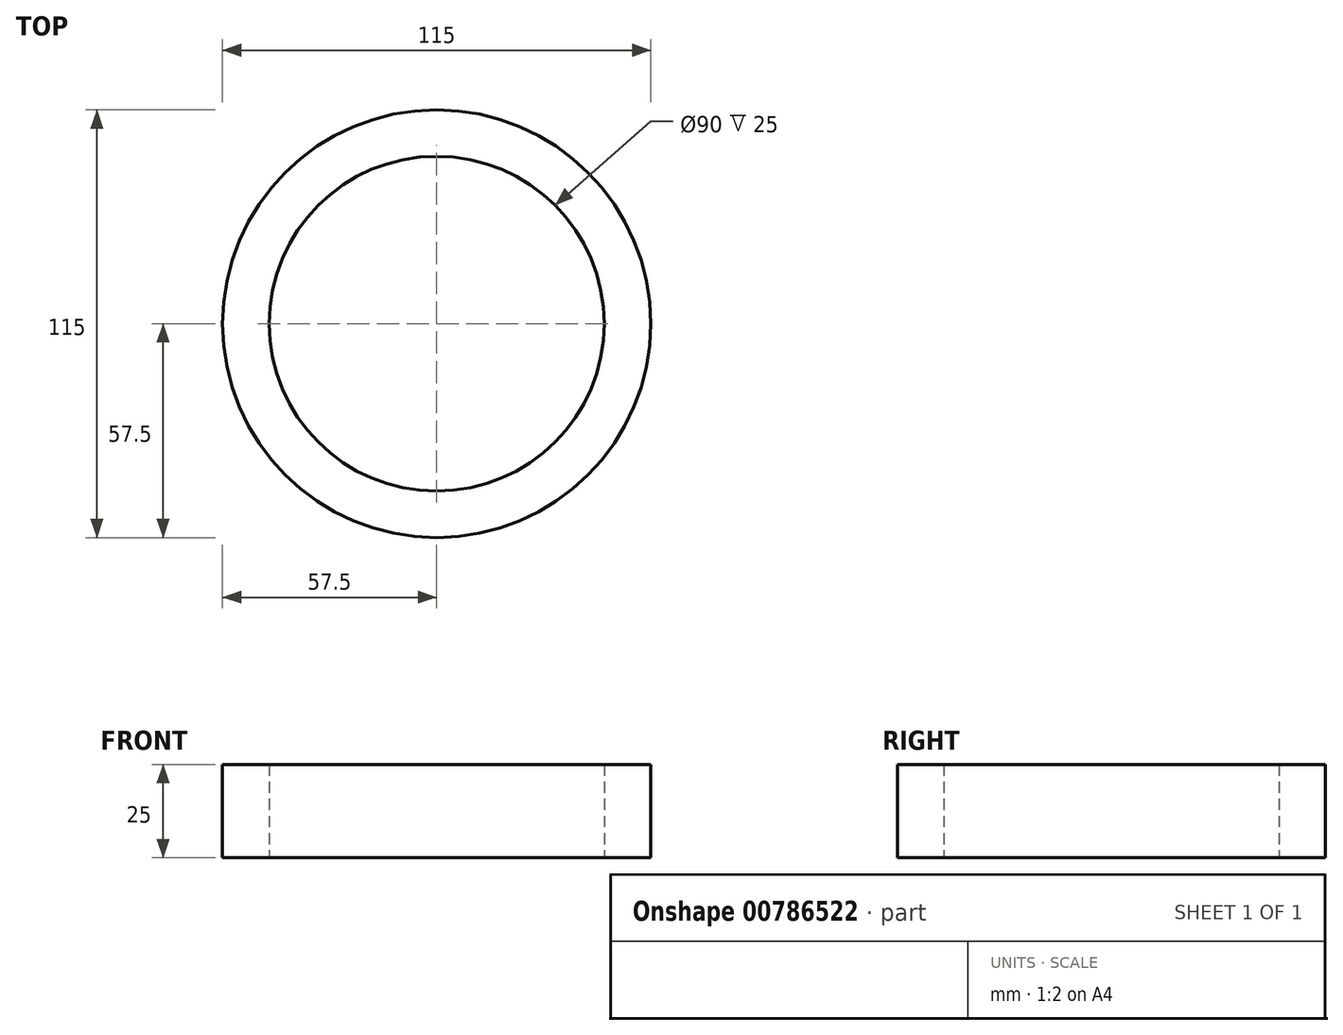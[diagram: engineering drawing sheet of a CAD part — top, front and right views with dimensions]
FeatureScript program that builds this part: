
annotation { "Feature Type Name" : "Feature", "Feature Type Description" : "" }
export const myFeature = defineFeature(function(context is Context, id is Id, definition is map)
    precondition{}
    {
        {
            var Q0;
            Q0=qCreatedBy(makeId("Top.planeOp"),FACE);
            var sketch = newSketch(context, id + "F0", { "sketchPlane" : qUnion([Q0])});
            skCircle(sketch, "E0", {"center": v(0, 0) * mm, "radius": 45 * mm});
            skCircle(sketch, "E1", {"center": v(0, 0) * mm, "radius": 57.5 * mm});
            skSolve(sketch);
        }
        {
            var Q0;
            Q0=makeQuery(id+"F0.imprint","IMPRINT",FACE,{"disambiguationData":[TD([[makeQuery(id+"F0.imprint","IMPRINT",EDGE,{"derivedFrom":sQuery(id+"F0.wireOp",EDGE,"E0")}),-1.0]])]});
            extrude(context, id + "F1", {"entities" : qUnion([Q0]), "depth" : 25 * mm, "offsetDistance" : 25 * mm});
        }
    });
